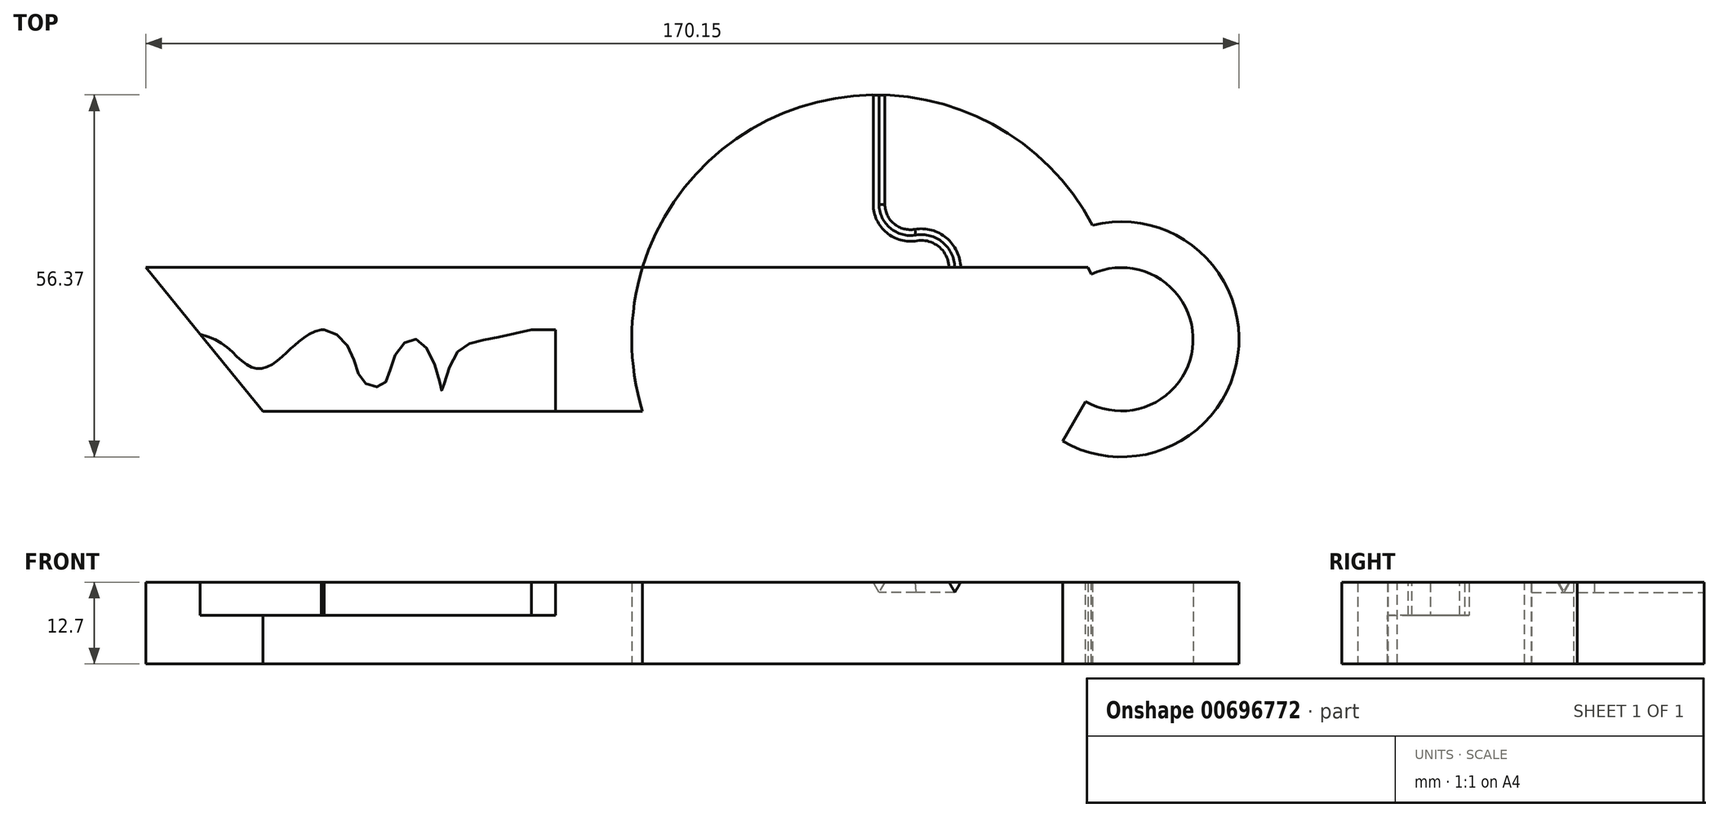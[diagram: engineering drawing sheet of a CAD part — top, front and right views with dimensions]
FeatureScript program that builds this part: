
annotation { "Feature Type Name" : "Feature", "Feature Type Description" : "" }
export const myFeature = defineFeature(function(context is Context, id is Id, definition is map)
    precondition{}
    {
        {
            var Q0;
            Q0=qCreatedBy(makeId("Top.planeOp"),FACE);
            var sketch = newSketch(context, id + "F0", { "sketchPlane" : qUnion([Q0])});
            skLineSegment(sketch, "E0", {"start": v(-76.55, 0) * mm, "end": v(76.12, 0) * mm});
            skLineSegment(sketch, "E1", {"start": v(0, 77.38) * mm, "end": v(0, -75.9) * mm});
            skLineSegment(sketch, "E2", {"start": v(0, 0) * mm, "end": v(76.12, 0) * mm});
            skLineSegment(sketch, "E3", {"start": v(38.06, 0) * mm, "end": v(38.06, 75.69) * mm});
            skCircle(sketch, "E4", {"center": v(38.06, 0) * mm, "radius": 38.06 * mm});
            skLineSegment(sketch, "E5.bottom", {"start": v(-75.64, 11.2) * mm, "end": v(74.43, 11.2) * mm});
            skLineSegment(sketch, "E5.top", {"start": v(-75.64, -11.2) * mm, "end": v(1.69, -11.2) * mm});
            skLineSegment(sketch, "E5.left", {"start": v(-75.64, 11.2) * mm, "end": v(-75.64, -11.2) * mm});
            skPoint(sketch, "E5.middle", {"position": v(0, 0) * mm});
            skSolve(sketch);
        }
        {
            var Q0;
            {var subQ0=sQuery(id+"F0.wireOp",EDGE,"E4");var subQ1=sQuery(id+"F0.wireOp",EDGE,"E3");var subQ2=makeQuery(id+"F0.imprint","INTERSECT",VERTEX,{"derivedFrom":[subQ1,subQ0]});Q0=makeQuery(id+"F0.imprint","IMPRINT",FACE,{"disambiguationData":[TD([[makeQuery(id+"F0.imprint","IMPRINT",EDGE,{"disambiguationData":[TD([[subQ2,1.0]])],"derivedFrom":subQ1}),1.0]])]});}
            var Q1;
            {var subQ0=sQuery(id+"F0.wireOp",EDGE,"E4");var subQ1=sQuery(id+"F0.wireOp",EDGE,"E3");var subQ2=makeQuery(id+"F0.imprint","INTERSECT",VERTEX,{"derivedFrom":[subQ1,subQ0]});Q1=makeQuery(id+"F0.imprint","IMPRINT",FACE,{"disambiguationData":[TD([[makeQuery(id+"F0.imprint","IMPRINT",EDGE,{"disambiguationData":[TD([[subQ2,1.0]])],"derivedFrom":subQ1}),-1.0]])]});}
            var Q2;
            {var subQ0=sQuery(id+"F0.wireOp",EDGE,"E4");var subQ1=sQuery(id+"F0.wireOp",EDGE,"E2");var subQ2=makeQuery(id+"F0.imprint","INTERSECT",VERTEX,{"derivedFrom":[subQ1,subQ0]});Q2=makeQuery(id+"F0.imprint","IMPRINT",FACE,{"disambiguationData":[TD([[makeQuery(id+"F0.imprint","IMPRINT",EDGE,{"disambiguationData":[TD([[subQ2,1.0]])],"derivedFrom":subQ1}),1.0]])]});}
            var Q3;
            {var subQ1=sQuery(id+"F0.wireOp",EDGE,"E2");var subQ3=sQuery(id+"F0.wireOp",EDGE,"E3");var subQ4=makeQuery(id+"F0.imprint","INTERSECT",VERTEX,{"derivedFrom":[subQ1,subQ3]});Q3=makeQuery(id+"F0.imprint","IMPRINT",FACE,{"disambiguationData":[TD([[makeQuery(id+"F0.imprint","IMPRINT",EDGE,{"disambiguationData":[TD([[subQ4,-1.0]])],"derivedFrom":subQ3}),1.0]])]});}
            var Q4;
            {var subQ0=sQuery(id+"F0.wireOp",EDGE,"E4");var subQ1=sQuery(id+"F0.wireOp",EDGE,"E2");var subQ4=makeQuery(id+"F0.imprint","INTERSECT",VERTEX,{"derivedFrom":[subQ1,subQ0]});Q4=makeQuery(id+"F0.imprint","IMPRINT",FACE,{"disambiguationData":[TD([[makeQuery(id+"F0.imprint","IMPRINT",EDGE,{"disambiguationData":[TD([[subQ4,1.0]])],"derivedFrom":subQ1}),-1.0]])]});}
            var Q5;
            {var subQ3=sQuery(id+"F0.wireOp",EDGE,"E5.left");var subQ5=sQuery(id+"F0.wireOp",EDGE,"E5.top");var subQ6=makeQuery(id+"F0.imprint","INTERSECT",VERTEX,{"derivedFrom":[subQ5,subQ3]});Q5=makeQuery(id+"F0.imprint","IMPRINT",FACE,{"disambiguationData":[TD([[makeQuery(id+"F0.imprint","IMPRINT",EDGE,{"disambiguationData":[TD([[subQ6,-1.0]])],"derivedFrom":subQ5}),1.0]])]});}
            var Q6;
            {var subQ3=sQuery(id+"F0.wireOp",EDGE,"E5.left");var subQ5=sQuery(id+"F0.wireOp",EDGE,"E5.bottom");var subQ7=makeQuery(id+"F0.imprint","INTERSECT",VERTEX,{"derivedFrom":[subQ5,subQ3]});Q6=makeQuery(id+"F0.imprint","IMPRINT",FACE,{"disambiguationData":[TD([[makeQuery(id+"F0.imprint","IMPRINT",EDGE,{"disambiguationData":[TD([[subQ7,-1.0]])],"derivedFrom":subQ5}),-1.0]])]});}
            var Q7;
            {var subQ1=sQuery(id+"F0.wireOp",EDGE,"E1");var subQ3=sQuery(id+"F0.wireOp",EDGE,"E5.bottom");var subQ4=makeQuery(id+"F0.imprint","INTERSECT",VERTEX,{"derivedFrom":[subQ1,subQ3]});Q7=makeQuery(id+"F0.imprint","IMPRINT",FACE,{"disambiguationData":[TD([[makeQuery(id+"F0.imprint","IMPRINT",EDGE,{"disambiguationData":[TD([[subQ4,-1.0]])],"derivedFrom":subQ3}),-1.0]])]});}
            var Q8;
            {var subQ0=sQuery(id+"F0.wireOp",EDGE,"E4");var subQ3=sQuery(id+"F0.wireOp",EDGE,"E5.top");var subQ5=makeQuery(id+"F0.imprint","INTERSECT",VERTEX,{"derivedFrom":[subQ0,subQ3]});Q8=makeQuery(id+"F0.imprint","IMPRINT",FACE,{"disambiguationData":[TD([[makeQuery(id+"F0.imprint","IMPRINT",EDGE,{"disambiguationData":[TD([[subQ5,1.0]])],"derivedFrom":subQ3}),1.0]])]});}
            extrude(context, id + "F1", {"entities" : qUnion([Q0, Q1, Q2, Q3, Q4, Q5, Q6, Q7, Q8]), "depth" : 12.7 * mm, "offsetDistance" : 25.4 * mm});
        }
        {
            var Q0;
            Q0=makeQuery(id+"F1.opExtrude","SWEPT_FACE",FACE,{"disambiguationData":[OSD([sQuery(id+"F0.wireOp",EDGE,"E5.top")])]});
            var sketch = newSketch(context, id + "F2", { "sketchPlane" : qUnion([Q0])});
            skPoint(sketch, "E6.oppositeSnap0", {"position": v(1.69, 6.35) * mm});
            skLineSegment(sketch, "E7.bottom", {"start": v(-75.64, 12.7) * mm, "end": v(-11.84, 12.7) * mm});
            skLineSegment(sketch, "E7.top", {"start": v(-75.64, 7.53) * mm, "end": v(-11.84, 7.53) * mm});
            skLineSegment(sketch, "E7.left", {"start": v(-75.64, 12.7) * mm, "end": v(-75.64, 7.53) * mm});
            skLineSegment(sketch, "E7.right", {"start": v(-11.84, 12.7) * mm, "end": v(-11.84, 7.53) * mm});
            skSolve(sketch);
        }
        {
            var Q0;
            Q0=qSketchRegion(id+"F2",true);
            extrude(context, id + "F3", {"entities" : qUnion([Q0]), "operationType" : NewBodyOperationType.REMOVE, "oppositeDirection" : true, "depth" : 12.7 * mm, "offsetDistance" : 25.4 * mm});
        }
        {
            var Q0;
            Q0=makeQuery(id+"F3.boolean.opBoolean","COPY",FACE,{"derivedFrom":makeQuery(id+"F3.opExtrude","SWEPT_FACE",FACE,{"disambiguationData":[OSD([sQuery(id+"F2.wireOp",EDGE,"E7.top")])]})});
            var sketch = newSketch(context, id + "F4", { "sketchPlane" : qUnion([Q0])});
            skPoint(sketch, "E8.8.internal.snap0", {"position": v(-43.74, 1.5) * mm});
            skFitSpline(sketch, "E8", {"points": [v(-71.4, 1.5) * mm, v(-64.86, 0) * mm, v(-61.37, -2.73) * mm, v(-58.75, -4.47) * mm, v(-56.14, -4.03) * mm, v(-53.52, -1.85) * mm, v(-51.34, 0) * mm, v(-47.85, 1.5) * mm, v(-43.74, -1.85) * mm, v(-41.75, -6.65) * mm, v(-38.7, -7.09) * mm, v(-36.95, -2.73) * mm, v(-33.46, 0) * mm, v(-29.98, -6.21) * mm, v(-29.54, -7.96) * mm, v(-27.36, -2.29) * mm, v(-22.56, 0) * mm, v(-15.59, 1.5) * mm], "startDerivative": vector(98.42, -12.85) * mm, "endDerivative": vector(95.91, 21.9) * mm});
            skLineSegment(sketch, "E9", {"start": v(-71.4, 1.5) * mm, "end": v(-15.59, 1.5) * mm});
            skSolve(sketch);
        }
        {
            var Q0;
            {var subQ0=sQuery(id+"F4.wireOp",EDGE,"E9");var subQ1=sQuery(id+"F4.wireOp",EDGE,"E8");var subQ3=makeQuery(id+"F4.imprint","INTERSECT",VERTEX,{"disambiguationData":[OD(0.0)],"derivedFrom":[subQ1,subQ0]});Q0=makeQuery(id+"F4.imprint","IMPRINT",FACE,{"disambiguationData":[TD([[makeQuery(id+"F4.imprint","IMPRINT",EDGE,{"disambiguationData":[TD([[subQ3,1.0]])],"derivedFrom":subQ1}),1.0]])]});}
            var Q1;
            {var subQ0=sQuery(id+"F4.wireOp",EDGE,"E9");var subQ1=sQuery(id+"F4.wireOp",EDGE,"E8");var subQ3=makeQuery(id+"F4.imprint","INTERSECT",VERTEX,{"disambiguationData":[OD(1.0)],"derivedFrom":[subQ1,subQ0]});Q1=makeQuery(id+"F4.imprint","IMPRINT",FACE,{"disambiguationData":[TD([[makeQuery(id+"F4.imprint","IMPRINT",EDGE,{"disambiguationData":[TD([[subQ3,-1.0]])],"derivedFrom":subQ1}),1.0]])]});}
            var Q2;
            Q2=makeQuery(id+"F1.opExtrude","CAP_FACE",FACE,{"disambiguationData":[OSD([sQuery(id+"F0.wireOp",EDGE,"E4"),sQuery(id+"F0.wireOp",EDGE,"E5.bottom"),sQuery(id+"F0.wireOp",EDGE,"E5.top"),sQuery(id+"F0.wireOp",EDGE,"E5.left")])],"isStart":false});
            extrude(context, id + "F5", {"entities" : qUnion([Q0, Q1]), "operationType" : NewBodyOperationType.ADD, "endBound" : BoundingType.UP_TO_SURFACE, "depth" : 25.4 * mm, "endBoundEntityFace" : qUnion([Q2]), "offsetDistance" : 25.4 * mm});
        }
        {
            var Q0;
            {var subQ0=sQuery(id+"F0.wireOp",EDGE,"E5.left");var subQ1=sQuery(id+"F0.wireOp",EDGE,"E5.top");var subQ2=sQuery(id+"F0.wireOp",EDGE,"E5.bottom");var subQ3=sQuery(id+"F0.wireOp",EDGE,"E4");Q0=makeQuery(id+"F5.boolean.opBoolean","MERGE",FACE,{"derivedFrom":[makeQuery(id+"F1.opExtrude","CAP_FACE",FACE,{"disambiguationData":[OSD([subQ3,subQ2,subQ1,subQ0])],"isStart":false}),makeQuery(id+"F5.opExtrude","CAP_FACE",FACE,{"disambiguationData":[OSD([subQ3,subQ2,subQ1,subQ0]),OD(0.0)],"isStart":false}),makeQuery(id+"F5.opExtrude","CAP_FACE",FACE,{"disambiguationData":[OSD([subQ3,subQ2,subQ1,subQ0]),OD(1.0)],"isStart":false})]});}
            var sketch = newSketch(context, id + "F6", { "sketchPlane" : qUnion([Q0])});
            skLineSegment(sketch, "E10", {"start": v(-54.4, -14.93) * mm, "end": v(-80.56, -12.75) * mm});
            skLineSegment(sketch, "E11", {"start": v(-80.56, -12.75) * mm, "end": v(-75.64, 11.2) * mm});
            skLineSegment(sketch, "E12", {"start": v(-75.64, 11.2) * mm, "end": v(-54.4, -14.93) * mm});
            skSolve(sketch);
        }
        {
            var Q0;
            Q0=qSketchRegion(id+"F6",true);
            extrude(context, id + "F7", {"entities" : qUnion([Q0]), "operationType" : NewBodyOperationType.REMOVE, "endBound" : BoundingType.THROUGH_ALL, "oppositeDirection" : true, "depth" : 25.4 * mm, "offsetDistance" : 25.4 * mm});
        }
        {
            var Q0;
            Q0=qCreatedBy(makeId("Right.planeOp"),FACE);
            cPlane(context, id + "F8", {"entities" : qUnion([Q0]), "cplaneType" : CPlaneType.OFFSET, "offset" : 76.2 * mm, "width" : 152.4 * mm, "height" : 152.4 * mm});
        }
        {
            var Q0;
            Q0=qCreatedBy(id+"F8.planeOp",FACE);
            var sketch = newSketch(context, id + "F9", { "sketchPlane" : qUnion([Q0])});
            skLineSegment(sketch, "E13", {"start": v(0, -5.67) * mm, "end": v(0, 19.48) * mm});
            skLineSegment(sketch, "E14.top", {"start": v(11.16, 0) * mm, "end": v(18.3, 0) * mm});
            skLineSegment(sketch, "E15", {"start": v(11.16, 0) * mm, "end": v(11.16, 12.7) * mm});
            skLineSegment(sketch, "E16", {"start": v(11.16, 12.7) * mm, "end": v(18.3, 12.7) * mm});
            skLineSegment(sketch, "E17", {"start": v(18.3, 12.7) * mm, "end": v(18.3, 0) * mm});
            skSolve(sketch);
        }
        {
            var Q0;
            Q0=makeQuery(id+"F9.imprint","IMPRINT",FACE,{"disambiguationData":[TD([[makeQuery(id+"F9.imprint","IMPRINT",EDGE,{"derivedFrom":sQuery(id+"F9.wireOp",EDGE,"E14.top")}),1.0]])]});
            var Q1;
            Q1=sQuery(id+"F9.wireOp",EDGE,"E13");
            revolve(context, id + "F10", {"operationType" : NewBodyOperationType.ADD, "entities" : qUnion([Q0]), "axis" : qUnion([Q1]), "revolveType" : RevolveType.TWO_DIRECTIONS, "angle" : 25 * degree, "angleBack" : 150 * degree});
        }
        {
            var Q0;
            Q0=qCreatedBy(makeId("Front.planeOp"),FACE);
            cPlane(context, id + "F11", {"entities" : qUnion([Q0]), "cplaneType" : CPlaneType.OFFSET, "offset" : 38.1 * mm, "width" : 152.4 * mm, "height" : 152.4 * mm});
        }
        {
            var Q0;
            {var subQ0=sQuery(id+"F0.wireOp",EDGE,"E5.left");var subQ1=sQuery(id+"F0.wireOp",EDGE,"E5.top");var subQ2=sQuery(id+"F0.wireOp",EDGE,"E5.bottom");var subQ3=sQuery(id+"F0.wireOp",EDGE,"E4");Q0=makeQuery(id+"F5.boolean.opBoolean","MERGE",FACE,{"derivedFrom":[makeQuery(id+"F1.opExtrude","CAP_FACE",FACE,{"disambiguationData":[OSD([subQ3,subQ2,subQ1,subQ0])],"isStart":false}),makeQuery(id+"F5.opExtrude","CAP_FACE",FACE,{"disambiguationData":[OSD([subQ3,subQ2,subQ1,subQ0]),OD(0.0)],"isStart":false}),makeQuery(id+"F5.opExtrude","CAP_FACE",FACE,{"disambiguationData":[OSD([subQ3,subQ2,subQ1,subQ0]),OD(1.0)],"isStart":false})]});}
            var sketch = newSketch(context, id + "F12", { "sketchPlane" : qUnion([Q0])});
            skLineSegment(sketch, "E18", {"start": v(38.5, -38.06) * mm, "end": v(38.5, -21.04) * mm});
            skArc(sketch, "E19", {"start": v(38.5, -21.04) * mm, "mid": v(40.22, -17.32) * mm, "end": v(44.17, -16.24) * mm});
            skArc(sketch, "E20", {"start": v(44.17, -16.24) * mm, "mid": v(48.62, -14.91) * mm, "end": v(50.28, -10.57) * mm});
            skLineSegment(sketch, "E21", {"start": v(50.28, -10.57) * mm, "end": v(50.28, 0) * mm});
            skLineSegment(sketch, "E22", {"start": v(0, 0) * mm, "end": v(43.3, 0) * mm});
            skLineSegment(sketch, "E23.MirrorCS", {"start": v(50.28, 10.57) * mm, "end": v(50.28, 0) * mm});
            skArc(sketch, "E24.MirrorCS", {"start": v(44.17, 16.24) * mm, "mid": v(48.62, 14.91) * mm, "end": v(50.28, 10.57) * mm});
            skArc(sketch, "E25.MirrorCS", {"start": v(38.5, 21.04) * mm, "mid": v(40.22, 17.32) * mm, "end": v(44.17, 16.24) * mm});
            skLineSegment(sketch, "E26.MirrorCS", {"start": v(38.5, 38.06) * mm, "end": v(38.5, 21.04) * mm});
            skSolve(sketch);
        }
        {
            var Q0;
            Q0=qCreatedBy(id+"F11.planeOp",FACE);
            var sketch = newSketch(context, id + "F13", { "sketchPlane" : qUnion([Q0])});
            skCircle(sketch, "E27.cCircle", {"center": v(38.5, 12.73) * mm, "radius": 1.6 * mm, "construction": true});
            skLineSegment(sketch, "E27.0", {"start": v(38.5, 11.14) * mm, "end": v(37.1, 13.53) * mm});
            skLineSegment(sketch, "E27.1", {"start": v(37.1, 13.53) * mm, "end": v(39.87, 13.53) * mm});
            skLineSegment(sketch, "E27.2", {"start": v(39.87, 13.53) * mm, "end": v(38.5, 11.14) * mm});
            skSolve(sketch);
        }
        {
            var Q0;
            Q0=makeQuery(id+"F13.imprint","IMPRINT",FACE,{"disambiguationData":[TD([[makeQuery(id+"F13.imprint","IMPRINT",EDGE,{"derivedFrom":sQuery(id+"F13.wireOp",EDGE,"E27.0")}),-1.0]])]});
            var Q1;
            Q1=sQuery(id+"F12.wireOp",EDGE,"E18");
            var Q2;
            Q2=sQuery(id+"F12.wireOp",EDGE,"E19");
            var Q3;
            Q3=sQuery(id+"F12.wireOp",EDGE,"E20");
            var Q4;
            Q4=sQuery(id+"F12.wireOp",EDGE,"E21");
            var Q5;
            Q5=sQuery(id+"F12.wireOp",EDGE,"E23.MirrorCS");
            var Q6;
            Q6=sQuery(id+"F12.wireOp",EDGE,"E24.MirrorCS");
            var Q7;
            Q7=sQuery(id+"F12.wireOp",EDGE,"E25.MirrorCS");
            var Q8;
            Q8=sQuery(id+"F12.wireOp",EDGE,"E26.MirrorCS");
            sweep(context, id + "F14", {"operationType" : NewBodyOperationType.REMOVE, "profiles" : qUnion([Q0]), "path" : qUnion([Q1, Q2, Q3, Q4, Q5, Q6, Q7, Q8])});
        }
    });
